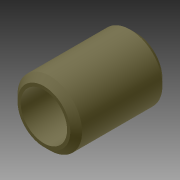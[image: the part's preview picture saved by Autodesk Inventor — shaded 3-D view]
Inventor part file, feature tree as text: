
AUTODESK INVENTOR PART (.ipt)
format: ipt  version: 2014 (Build 180170000, 170)  size: 112,128 bytes
history: native  units: in
note: dims shown in document units (in); Inventor stores cm internally (conversion verified against a paired STEP export)
features: other x35, revolve x1, sketch x1
ambient origin geometry x8: Origin, YZ Plane, XZ Plane, XY Plane, X Axis, Y Axis, Z Axis, Center Point
bodies: Solid1 (feature_tree)
feature tree (37):
  revolve  "Revolution1"  [1 undecoded]
  other  "bushing_XY"
  other  "bushing_YZ"
  other  "bushing_ZX"
  other  "bushing_X"
  other  "bushing_Y"
  other  "bushing_Z"
  other  "bushing_Center"
  other  "id1_XY"
  other  "id1_YZ"
  other  "id1_ZX"
  other  "id1_X"
  other  "id1_Y"
  other  "id1_Z"
  other  "id1_Center"
  other  "id2_XY"
  other  "id2_YZ"
  other  "id2_ZX"
  other  "id2_X"
  other  "id2_Y"
  other  "id2_Z"
  other  "id2_Center"
  other  "id3_XY"
  other  "id3_YZ"
  other  "id3_ZX"
  other  "id3_X"
  other  "id3_Y"
  other  "id3_Z"
  other  "id3_Center"
  other  "id4_XY"
  other  "id4_YZ"
  other  "id4_ZX"
  other  "id4_X"
  other  "id4_Y"
  other  "id4_Z"
  other  "id4_Center"
  sketch  "Sketch_1"  dims[d0=360.0deg]
note: 1 required parameter value undecoded (feature->parameter linkage not recoverable at this tier; creation-order binding heuristic only, values carry confidence <= 0.55)
